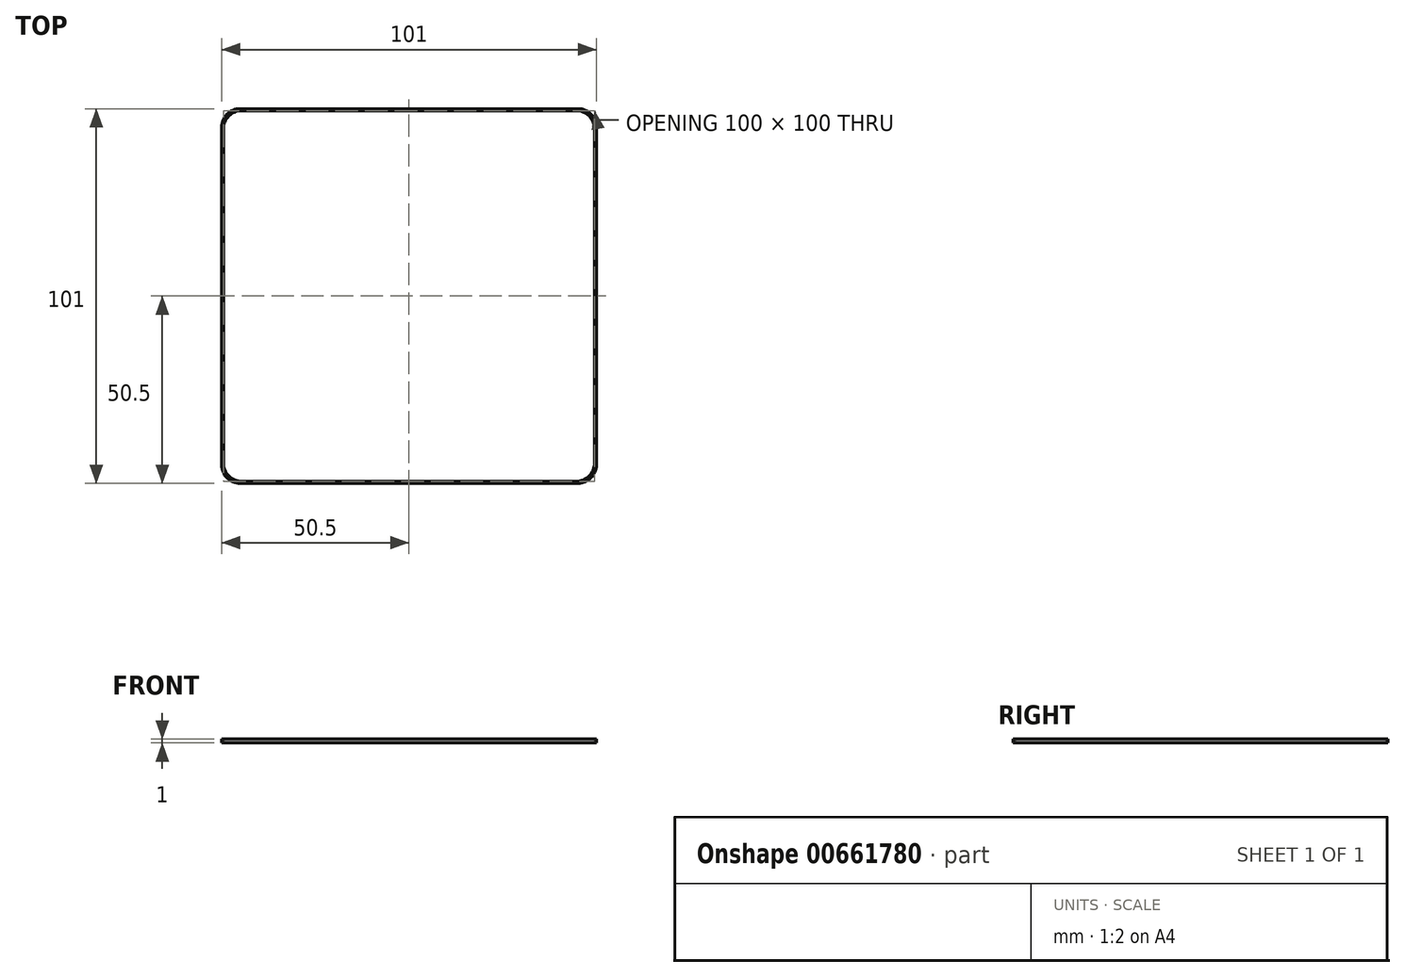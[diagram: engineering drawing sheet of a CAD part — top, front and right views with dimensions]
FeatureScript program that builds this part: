
annotation { "Feature Type Name" : "Feature", "Feature Type Description" : "" }
export const myFeature = defineFeature(function(context is Context, id is Id, definition is map)
    precondition{}
    {
        {
            var Q0;
            Q0=qCreatedBy(makeId("Top.planeOp"),FACE);
            var sketch = newSketch(context, id + "F0", { "sketchPlane" : qUnion([Q0])});
            skLineSegment(sketch, "E0.bottom", {"start": v(45, -50) * mm, "end": v(-45, -50) * mm});
            skLineSegment(sketch, "E0.top", {"start": v(45, 50) * mm, "end": v(-45, 50) * mm});
            skLineSegment(sketch, "E0.left", {"start": v(50, -45) * mm, "end": v(50, 45) * mm});
            skLineSegment(sketch, "E0.right", {"start": v(-50, -45) * mm, "end": v(-50, 45) * mm});
            skPoint(sketch, "E0.middle", {"position": v(0, 0) * mm});
            skLineSegment(sketch, "E1.bottom", {"start": v(45.5, -50.5) * mm, "end": v(-45.5, -50.5) * mm});
            skLineSegment(sketch, "E1.top", {"start": v(45.5, 50.5) * mm, "end": v(-45.5, 50.5) * mm});
            skLineSegment(sketch, "E1.left", {"start": v(50.5, -45.5) * mm, "end": v(50.5, 45.5) * mm});
            skLineSegment(sketch, "E1.right", {"start": v(-50.5, -45.5) * mm, "end": v(-50.5, 45.5) * mm});
            skPoint(sketch, "E2.visualSharp", {"position": v(-50, 50) * mm});
            skArc(sketch, "E2.filletArc", {"start": v(-45, 50) * mm, "mid": v(-48.54, 48.54) * mm, "end": v(-50, 45) * mm});
            skPoint(sketch, "E3.visualSharp", {"position": v(-50.5, 50.5) * mm});
            skArc(sketch, "E3.filletArc", {"start": v(-45.5, 50.5) * mm, "mid": v(-49.04, 49.04) * mm, "end": v(-50.5, 45.5) * mm});
            skPoint(sketch, "E4.visualSharp", {"position": v(50, 50) * mm});
            skArc(sketch, "E4.filletArc", {"start": v(50, 45) * mm, "mid": v(48.54, 48.54) * mm, "end": v(45, 50) * mm});
            skPoint(sketch, "E5.visualSharp", {"position": v(50.5, 50.5) * mm});
            skArc(sketch, "E5.filletArc", {"start": v(50.5, 45.5) * mm, "mid": v(49.04, 49.04) * mm, "end": v(45.5, 50.5) * mm});
            skPoint(sketch, "E6.visualSharp", {"position": v(50, -50) * mm});
            skArc(sketch, "E6.filletArc", {"start": v(45, -50) * mm, "mid": v(48.54, -48.54) * mm, "end": v(50, -45) * mm});
            skPoint(sketch, "E7.visualSharp", {"position": v(50.5, -50.5) * mm});
            skArc(sketch, "E7.filletArc", {"start": v(45.5, -50.5) * mm, "mid": v(49.04, -49.04) * mm, "end": v(50.5, -45.5) * mm});
            skPoint(sketch, "E8.visualSharp", {"position": v(-50, -50) * mm});
            skArc(sketch, "E8.filletArc", {"start": v(-50, -45) * mm, "mid": v(-48.54, -48.54) * mm, "end": v(-45, -50) * mm});
            skPoint(sketch, "E9.visualSharp", {"position": v(-50.5, -50.5) * mm});
            skArc(sketch, "E9.filletArc", {"start": v(-50.5, -45.5) * mm, "mid": v(-49.04, -49.04) * mm, "end": v(-45.5, -50.5) * mm});
            skSolve(sketch);
        }
        {
            var Q0;
            Q0=makeQuery(id+"F0.imprint","IMPRINT",FACE,{"disambiguationData":[TD([[makeQuery(id+"F0.imprint","IMPRINT",EDGE,{"derivedFrom":sQuery(id+"F0.wireOp",EDGE,"E0.bottom")}),1.0]])]});
            extrude(context, id + "F1", {"entities" : qUnion([Q0]), "depth" : 1 * mm, "offsetDistance" : 25 * mm});
        }
    });
